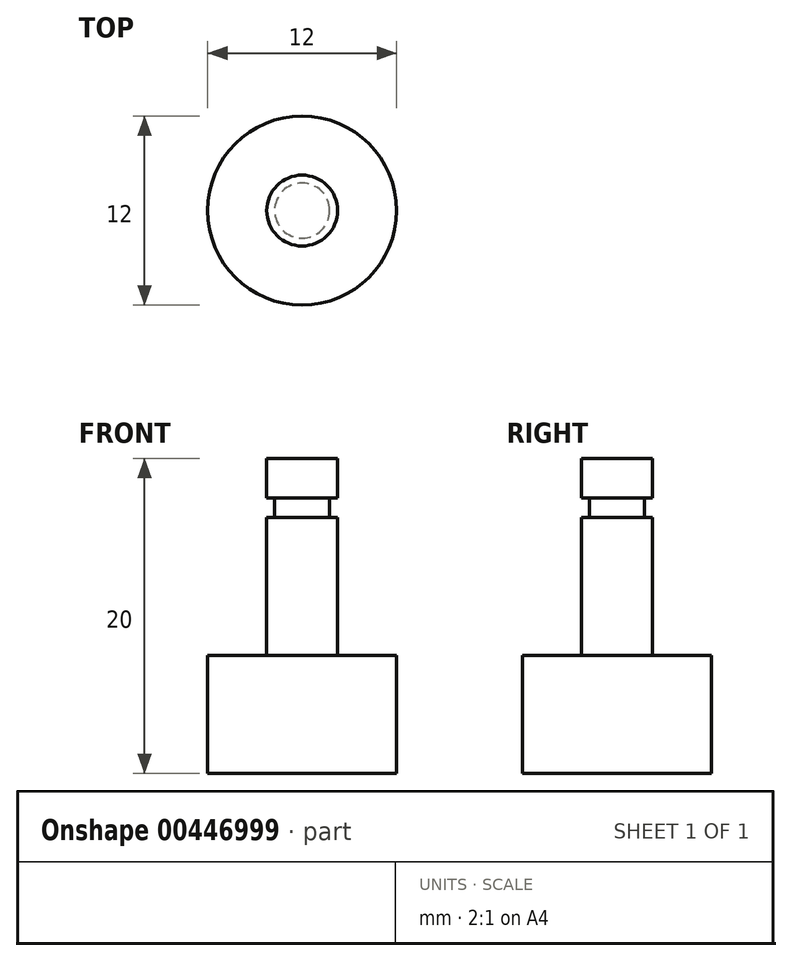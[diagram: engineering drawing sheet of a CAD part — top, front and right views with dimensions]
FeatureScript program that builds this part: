
annotation { "Feature Type Name" : "Feature", "Feature Type Description" : "" }
export const myFeature = defineFeature(function(context is Context, id is Id, definition is map)
    precondition{}
    {
        {
            var Q0;
            Q0=qCreatedBy(makeId("Front.planeOp"),FACE);
            var sketch = newSketch(context, id + "F0", { "sketchPlane" : qUnion([Q0])});
            skLineSegment(sketch, "E0.bottom", {"start": v(-6, 3.75) * mm, "end": v(6, 3.75) * mm});
            skLineSegment(sketch, "E0.top", {"start": v(-6, -3.75) * mm, "end": v(6, -3.75) * mm});
            skLineSegment(sketch, "E0.left", {"start": v(-6, 3.75) * mm, "end": v(-6, -3.75) * mm});
            skLineSegment(sketch, "E0.right", {"start": v(6, 3.75) * mm, "end": v(6, -3.75) * mm});
            skPoint(sketch, "E0.middle", {"position": v(0, 0) * mm});
            skLineSegment(sketch, "E1.bottom", {"start": v(2.25, 3.75) * mm, "end": v(-2.25, 3.75) * mm});
            skLineSegment(sketch, "E1.top", {"start": v(2.25, 16.25) * mm, "end": v(-2.25, 16.25) * mm});
            skLineSegment(sketch, "E1.left", {"start": v(2.25, 3.75) * mm, "end": v(2.25, 16.25) * mm});
            skLineSegment(sketch, "E1.right", {"start": v(-2.25, 3.75) * mm, "end": v(-2.25, 16.25) * mm});
            skLineSegment(sketch, "E2", {"start": v(-2.25, 13.75) * mm, "end": v(2.25, 13.75) * mm});
            skLineSegment(sketch, "E3", {"start": v(-2.25, 12.5) * mm, "end": v(2.25, 12.5) * mm});
            skLineSegment(sketch, "E4", {"start": v(-1.75, 13.75) * mm, "end": v(-1.75, 12.5) * mm});
            skLineSegment(sketch, "E5", {"start": v(1.75, 13.75) * mm, "end": v(1.75, 12.5) * mm});
            skPoint(sketch, "E6.end.orphan", {"position": v(0, 3.75) * mm});
            skLineSegment(sketch, "E7", {"start": v(0, -3.75) * mm, "end": v(0, 16.25) * mm});
            skSolve(sketch);
        }
        {
            var Q0;
            {var subQ0=sQuery(id+"F0.wireOp",EDGE,"E4");Q0=makeQuery(id+"F0.imprint","IMPRINT",FACE,{"disambiguationData":[TD([[makeQuery(id+"F0.imprint","IMPRINT",EDGE,{"derivedFrom":subQ0}),1.0]])]});}
            var Q1;
            {var subQ4=sQuery(id+"F0.wireOp",EDGE,"E1.right");var subQ6=sQuery(id+"F0.wireOp",EDGE,"E1.top");var subQ7=makeQuery(id+"F0.imprint","INTERSECT",VERTEX,{"derivedFrom":[subQ6,subQ4]});Q1=makeQuery(id+"F0.imprint","IMPRINT",FACE,{"disambiguationData":[TD([[makeQuery(id+"F0.imprint","IMPRINT",EDGE,{"disambiguationData":[TD([[subQ7,1.0]])],"derivedFrom":subQ6}),1.0]])]});}
            var Q2;
            {var subQ0=sQuery(id+"F0.wireOp",EDGE,"E3");var subQ4=sQuery(id+"F0.wireOp",EDGE,"E1.right");var subQ5=makeQuery(id+"F0.imprint","INTERSECT",VERTEX,{"derivedFrom":[subQ4,subQ0]});Q2=makeQuery(id+"F0.imprint","IMPRINT",FACE,{"disambiguationData":[TD([[makeQuery(id+"F0.imprint","IMPRINT",EDGE,{"disambiguationData":[TD([[subQ5,-1.0]])],"derivedFrom":subQ0}),-1.0]])]});}
            var Q3;
            {var subQ0=sQuery(id+"F0.wireOp",EDGE,"E0.left");Q3=makeQuery(id+"F0.imprint","IMPRINT",FACE,{"disambiguationData":[TD([[makeQuery(id+"F0.imprint","IMPRINT",EDGE,{"derivedFrom":subQ0}),1.0]])]});}
            var Q4;
            Q4=sQuery(id+"F0.wireOp",EDGE,"E7");
            revolve(context, id + "F1", {"entities" : qUnion([Q0, Q1, Q2, Q3]), "axis" : qUnion([Q4]), "revolveType" : RevolveType.FULL});
        }
    });
